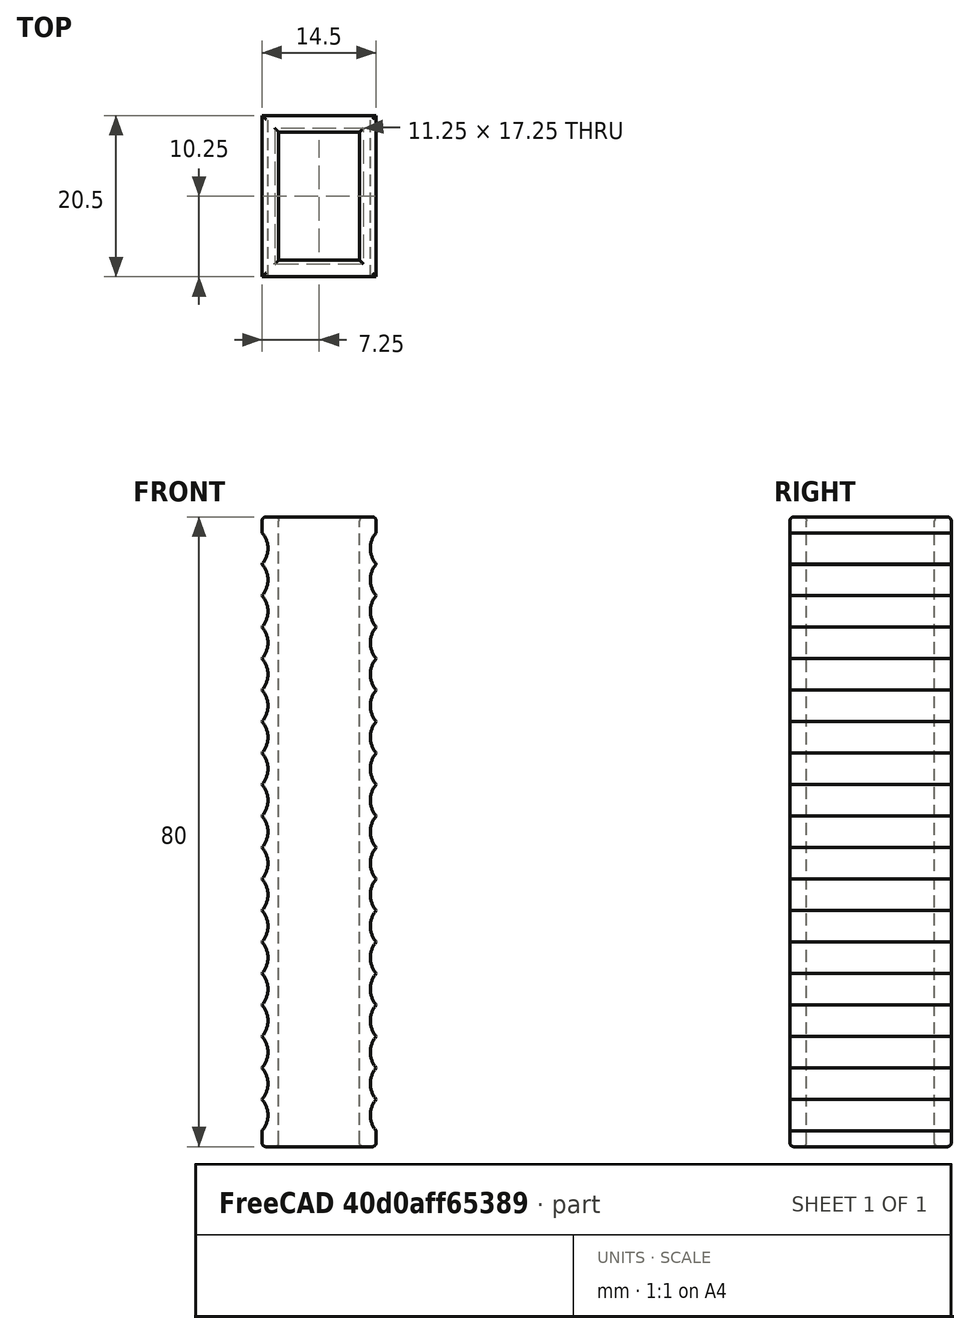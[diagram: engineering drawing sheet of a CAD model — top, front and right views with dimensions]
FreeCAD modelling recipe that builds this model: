
FCSTD DOCUMENT  (FreeCAD 0.15R4671 (Git))
Label: soft_finger_sleeve
License: All rights reserved
LicenseURL: http://en.wikipedia.org/wiki/All_rights_reserved
objects: Part::Cylinder×19, Part::Box×2, Part::Cut×2, Part::MultiFuse×2, Part::Fillet×1, Part::Mirroring×1
note: 27 computed .brp shape members not serialized (recipe doc carries the construction recipe); baked Part::Feature solids carry a one-line shape summary decoded from their .brp

FEATURE [Part::Box] Box  label="Cube"
  Height = 80
  Length = 14.5
  Width = 20.5
FEATURE [Part::Box] Box001  label="Cube001"
  Height = 80
  Length = 10.25
  Placement = pos=(2.125,2.125,0) rot=(0,0,1;0rad)
  Width = 16.25
FEATURE [Part::Cut] Cut
  Base = -> Box
  Tool = -> Box001
FEATURE [Part::Fillet] Fillet
  Base = -> Cut
  Edges = 16 edges r=0.5: [Edge2,Edge4,Edge5,Edge7,Edge8,Edge9,Edge10,Edge11,Edge12,Edge13,Edge14,Edge16,Edge17,Edge18,Edge19,Edge20]
FEATURE [Part::Cylinder] Cylinder
  Angle = 360
  Height = 50
  Placement = pos=(-2.25,-15,4) rot=(-1,0,0;1.5708rad)
  Radius = 3
FEATURE [Part::Cylinder] Cylinder001 .. Cylinder018  x18 (patterned run collapsed; names and placements below)
  Angle = 360
  Height = 50
  Radius = 3
  placements: 18 in arithmetic series — first pos=(-2.25,-15,8) rot=(-1,0,0;1.5708rad), step (0,0,4), last pos=(-2.25,-15,76) rot=(-1,0,0;1.5708rad)
FEATURE [Part::MultiFuse] Fusion
  Shapes = -> [Cylinder018,Cylinder010,Cylinder,Cylinder008,Cylinder005,Cylinder001,Cylinder004,Cylinder006,Cylinder014,Cylinder015,Cylinder011,Cylinder013,Cylinder007,Cylinder012,Cylinder003,Cylinder002,Cylinder017,Cylinder009,Cylinder016]
FEATURE [Part::Mirroring] Part__Mirroring  label="Fusion (Mirror #1)"
  Base = (7.25,0,0)
  Normal = (1,0,0)
  Source = -> Fusion
FEATURE [Part::MultiFuse] Fusion001
  Shapes = -> [Part__Mirroring,Fusion]
FEATURE [Part::Cut] Cut001
  Base = -> Fillet
  Tool = -> Fusion001
